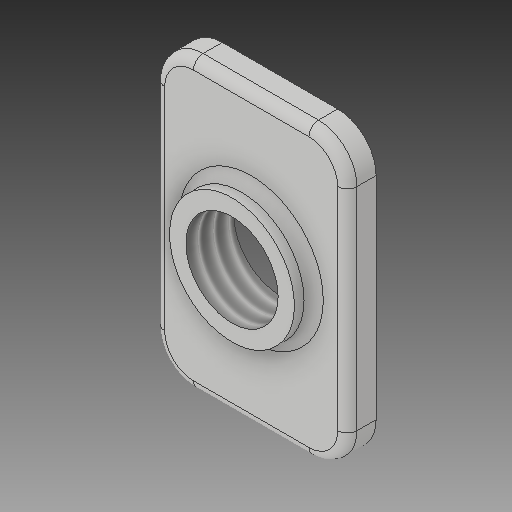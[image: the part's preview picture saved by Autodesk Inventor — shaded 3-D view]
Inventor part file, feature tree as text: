
AUTODESK INVENTOR PART (.ipt)
format: ipt  version: 2018 (Build 220112000, 112)  size: 178,176 bytes
history: native  units: mm
features: other x3, sketch x2
ambient origin geometry x8: Origin, YZ Plane, XZ Plane, XY Plane, X Axis, Y Axis, Z Axis, Center Point
bodies: Solid1 (feature_tree)
feature tree (5):
  other  "M5 Tee Nut-Generic_MIR_CPY_CPY.ipt"
  other  "Solid1::M5 Tee Nut-Generic_MIR_CPY_CPY.ipt"
  other  "TaggingFeature1"
  sketch  "Sketch1"  dims[d0=10.0mm]
  sketch  "Sketch2"
